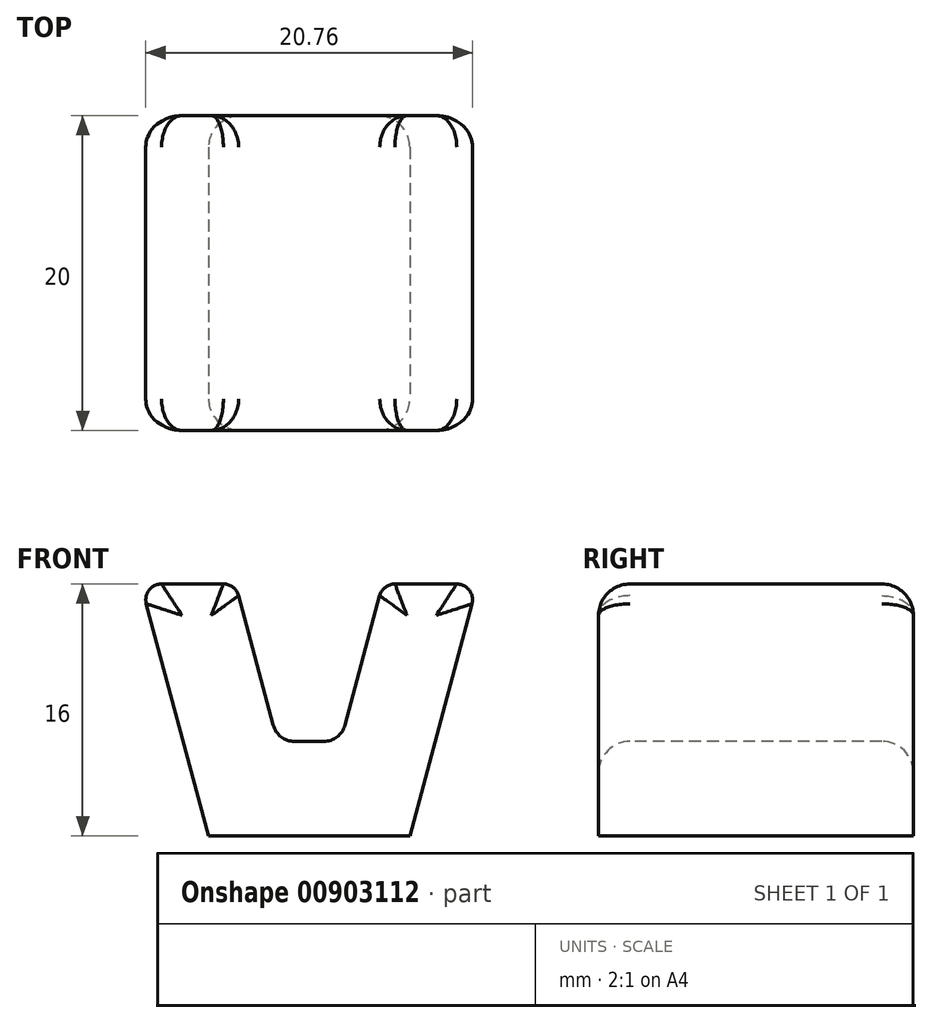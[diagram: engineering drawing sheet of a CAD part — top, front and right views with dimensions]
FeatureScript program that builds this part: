
annotation { "Feature Type Name" : "Feature", "Feature Type Description" : "" }
export const myFeature = defineFeature(function(context is Context, id is Id, definition is map)
    precondition{}
    {
        {
            var Q0;
            Q0=qCreatedBy(makeId("Top.planeOp"),FACE);
            var sketch = newSketch(context, id + "F0", { "sketchPlane" : qUnion([Q0])});
            skLineSegment(sketch, "E0.bottom", {"start": v(12.5, -12.5) * mm, "end": v(-12.5, -12.5) * mm});
            skLineSegment(sketch, "E0.top", {"start": v(12.5, 12.5) * mm, "end": v(-12.5, 12.5) * mm});
            skLineSegment(sketch, "E0.left", {"start": v(12.5, -12.5) * mm, "end": v(12.5, 12.5) * mm});
            skLineSegment(sketch, "E0.right", {"start": v(-12.5, -12.5) * mm, "end": v(-12.5, 12.5) * mm});
            skPoint(sketch, "E0.middle", {"position": v(0, 0) * mm});
            skPoint(sketch, "E1.visualSharp", {"position": v(-12.5, -12.5) * mm});
            skPoint(sketch, "E2.visualSharp", {"position": v(-12.5, 12.5) * mm});
            skPoint(sketch, "E3.visualSharp", {"position": v(12.5, 12.5) * mm});
            skPoint(sketch, "E4.visualSharp", {"position": v(12.5, -12.5) * mm});
            skSolve(sketch);
        }
        {
            var Q0;
            Q0=qCreatedBy(makeId("Front.planeOp"),FACE);
            var sketch = newSketch(context, id + "F1", { "sketchPlane" : qUnion([Q0])});
            skLineSegment(sketch, "E5", {"start": v(0, 6) * mm, "end": v(-0.93, 6) * mm});
            skLineSegment(sketch, "E6", {"start": v(0, 6) * mm, "end": v(0.93, 6) * mm});
            skLineSegment(sketch, "E7", {"start": v(-4.48, 15.26) * mm, "end": v(-2.28, 7.04) * mm});
            skLineSegment(sketch, "E8", {"start": v(4.48, 15.26) * mm, "end": v(2.28, 7.04) * mm});
            skPoint(sketch, "E9.visualSharp", {"position": v(2, 6) * mm});
            skArc(sketch, "E9.filletArc", {"start": v(0.93, 6) * mm, "mid": v(1.78, 6.29) * mm, "end": v(2.28, 7.04) * mm});
            skPoint(sketch, "E10.visualSharp", {"position": v(-2, 6) * mm});
            skArc(sketch, "E10.filletArc", {"start": v(-2.28, 7.04) * mm, "mid": v(-1.78, 6.29) * mm, "end": v(-0.93, 6) * mm});
            skLineSegment(sketch, "E11", {"start": v(2.28, 7.04) * mm, "end": v(17.08, 7.04) * mm, "construction": true});
            skLineSegment(sketch, "E12", {"start": v(10.34, 14.74) * mm, "end": v(6.4, 0) * mm});
            skLineSegment(sketch, "E13", {"start": v(4.68, 16) * mm, "end": v(-4.68, 16) * mm, "construction": true});
            skLineSegment(sketch, "E14", {"start": v(-10.34, 14.74) * mm, "end": v(-6.4, 0) * mm});
            skLineSegment(sketch, "E15", {"start": v(9.38, 16) * mm, "end": v(5.45, 16) * mm});
            skLineSegment(sketch, "E16", {"start": v(-5.45, 16) * mm, "end": v(-9.38, 16) * mm});
            skLineSegment(sketch, "E17", {"start": v(6.4, 0) * mm, "end": v(-6.4, 0) * mm});
            skPoint(sketch, "E18.visualSharp", {"position": v(-10.68, 16) * mm});
            skArc(sketch, "E18.filletArc", {"start": v(-9.38, 16) * mm, "mid": v(-10.17, 15.6) * mm, "end": v(-10.34, 14.74) * mm});
            skPoint(sketch, "E19.visualSharp", {"position": v(-4.68, 16) * mm});
            skArc(sketch, "E19.filletArc", {"start": v(-4.48, 15.26) * mm, "mid": v(-4.84, 15.8) * mm, "end": v(-5.45, 16) * mm});
            skPoint(sketch, "E20.visualSharp", {"position": v(4.68, 16) * mm});
            skArc(sketch, "E20.filletArc", {"start": v(5.45, 16) * mm, "mid": v(4.84, 15.8) * mm, "end": v(4.48, 15.26) * mm});
            skPoint(sketch, "E21.visualSharp", {"position": v(10.68, 16) * mm});
            skArc(sketch, "E21.filletArc", {"start": v(10.34, 14.74) * mm, "mid": v(10.17, 15.6) * mm, "end": v(9.38, 16) * mm});
            skSolve(sketch);
        }
        {
            var Q0;
            Q0=makeQuery(id+"F1.imprint","IMPRINT",FACE,{"disambiguationData":[TD([[makeQuery(id+"F1.imprint","IMPRINT",EDGE,{"derivedFrom":sQuery(id+"F1.wireOp",EDGE,"E5")}),1.0]])]});
            extrude(context, id + "F2", {"entities" : qUnion([Q0]), "endBound" : BoundingType.SYMMETRIC, "oppositeDirection" : true, "depth" : 20 * mm});
        }
        {
            var Q0;
            Q0=makeQuery(id+"F2.opExtrude","CAP_EDGE",EDGE,{"disambiguationData":[OSD([sQuery(id+"F1.wireOp",EDGE,"E14")])],"isStart":true});
            var Q1;
            Q1=makeQuery(id+"F2.opExtrude","CAP_EDGE",EDGE,{"disambiguationData":[OSD([sQuery(id+"F1.wireOp",EDGE,"E14")])],"isStart":false});
            fillet(context, id + "F3", {"entities" : qUnion([Q0, Q1]), "radius" : 2 * mm, "tangentPropagation" : true, "allowEdgeOverflow" : false});
        }
    });
